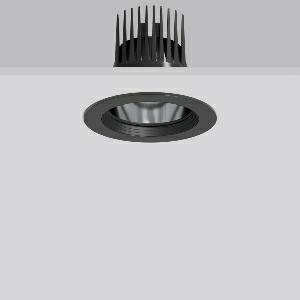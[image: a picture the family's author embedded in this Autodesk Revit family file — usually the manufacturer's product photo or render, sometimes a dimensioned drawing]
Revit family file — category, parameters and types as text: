
# Revit family: heledon_maxi_e_901780_003_f62e
name_source: partatom
category: Lighting Fixtures
units: mm (PartAtom-declared; Revit-internal decimal feet)

## family parameters
Cut with Voids When Loaded = No
Host = Face
Light Source = No
Part Type = Normal
Room Calculation Point = No
Round Connector Dimension = Use Diameter
Shared = No

## types (1)
- HELEDON maxi E (1 x LED Modul 920 meat+, 2150 lm, 2000)
    Apparent Load = 33 VA
    Approval mark = CE
    CIE Flux Codes = 96 100 100 100 100
    Color Rendering = 90
    Color Temperature = 2000
    Default Elevation = 1800 mm
    Description = Series: HELEDON maxi
Round recessed downlight. Housing: die-cast aluminium, powder-coated. Black plastic ring and recessed LED to prevent glare from the side. Optical assembly with reflector made of MIRO-Silver with 98% total light reflection for outstanding efficiency - can be changed without tools. Special LED for illumination of meat included. Suitable for Recessed ceiling mounting. Installation without tools thanks to spring fastening system. Including separate LED converter with connecting cable 600 mm.High quality converter without flickering and stroboscopic effect. Through-wiring box (5 pole) available as accessory. The following accessories can be mounted without use of tools: interchangeable lenses, decorative glasses, honeycomb louvre, clear and frosted diffusers, white interchangeable plastic ring. 
Colour: deep black, matt (RAL 9005)
Diameter: 162 mm
Height: 3 mm
Cut-out diameter: 152 mm
Recess height: 200 mm
Luminaire: recess height: 135 mm
Lamp: LED
Socket: without socket
Colour temperature: meat +
System power: 33 W
Rated luminous flux: 2150 lm
Luminous efficiency: 65 lm/W
Control gear: Regulated power supply
Protection class: II
Type of protection: IP 20
    Height = 0 mm  [stored 0 ft]
    Lamp = 1 x LED Modul 920 meat+
    Lamp Light Flux = 2150 lm
    Lamp count = 1
    Length = 162 mm
    Lifetime = 50000 h
    Luminous efficacy = 65 lm/W
    Manufacturer = RZB
    ModVariant = No
    Model = 901780.003
    Mounting Place = Ceiling
    Mounting Type = Recessed
    Number of Poles = 1
    OnlyDefault = Yes
    Power Factor = 1
    Product Name = HELEDON maxi E
    Product group = Recessed downlights
    ProductGroupID = 402
    Protection Class = Protection class II
    Protection Degree = IP 20
    RLX_Detail_Level = 1
    RLX_Emergency_Light_Flux = 0 lm
    RLX_Emergency_Type = 0
    RLX_Emergency_Type_DB = No
    RlxData = <blob elided: 122361 chars, md5=bcbc81e8>
    Socket = socket
    Standby Power = 0 W
    System Light Flux = 2150 lm
    System Power = 33 W
    Type Comments = Product without accessories
    Type Image = 901662.003.jpg
    URL = http://relux.com
    VarID = ---
    Voltage = 230 V
    Voltage Range = 220-240 V
    Weight = 0.00 kg
    Width = 0 mm  [stored 0 ft]

note: [stored X ft] marks values corroborated as IEEE doubles in the binary element streams (Revit-internal decimal feet)

## geometry (parser evidence)
native form markers: Blend x4, Sweep x11
no freeform markers — native parametric forms only
